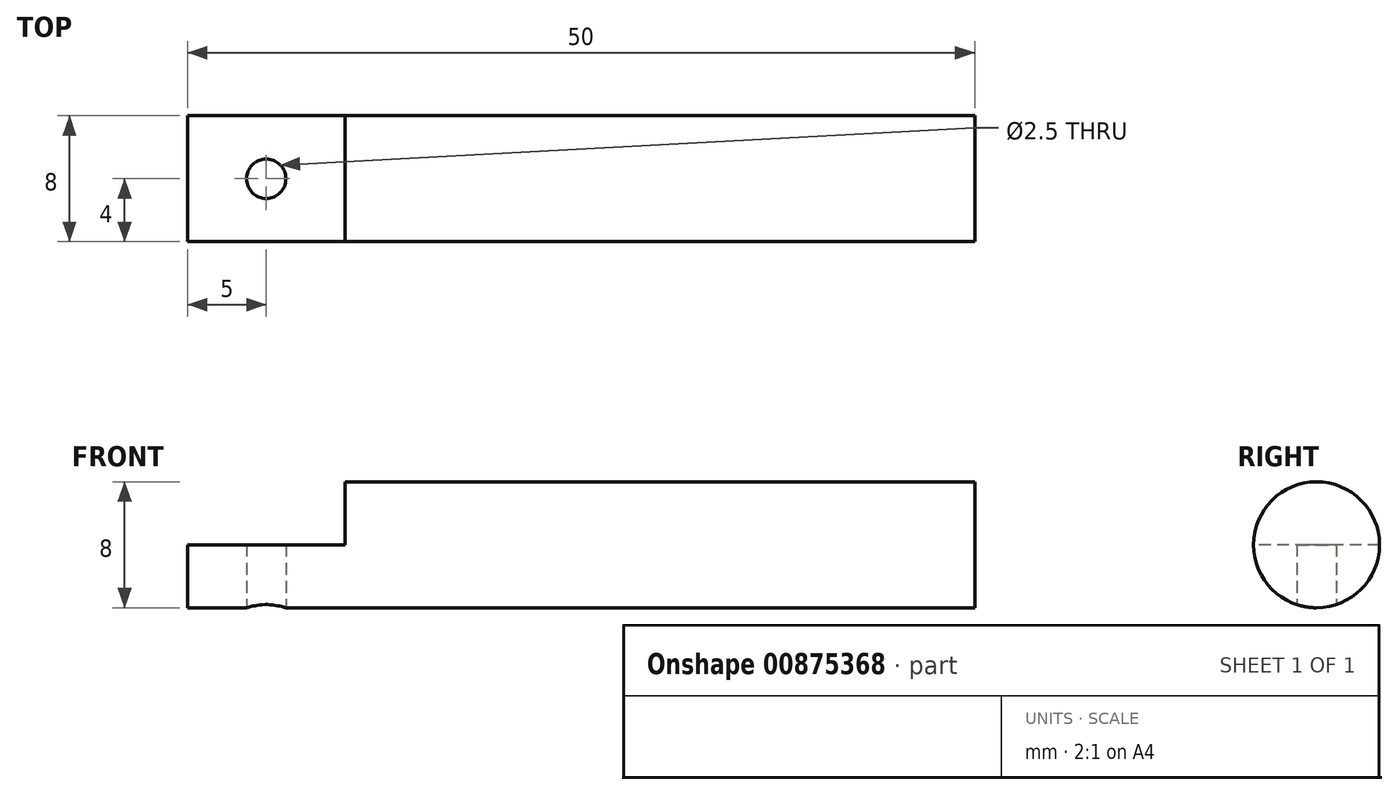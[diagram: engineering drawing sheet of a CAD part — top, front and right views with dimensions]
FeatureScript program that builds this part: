
annotation { "Feature Type Name" : "Feature", "Feature Type Description" : "" }
export const myFeature = defineFeature(function(context is Context, id is Id, definition is map)
    precondition{}
    {
        {
            var Q0;
            Q0=qCreatedBy(makeId("Right.planeOp"),FACE);
            var sketch = newSketch(context, id + "F0", { "sketchPlane" : qUnion([Q0])});
            skCircle(sketch, "E0", {"center": v(0, 0) * mm, "radius": 4 * mm});
            skSolve(sketch);
        }
        {
            var Q0;
            Q0=makeQuery(id+"F0.imprint","IMPRINT",FACE,{"disambiguationData":[TD([[makeQuery(id+"F0.imprint","IMPRINT",EDGE,{"derivedFrom":sQuery(id+"F0.wireOp",EDGE,"E0")}),1.0]])]});
            extrude(context, id + "F1", {"entities" : qUnion([Q0]), "depth" : 40 * mm, "offsetDistance" : 25 * mm});
        }
        {
            var Q0;
            Q0=makeQuery(id+"F1.opExtrude","CAP_FACE",FACE,{"disambiguationData":[OSD([sQuery(id+"F0.wireOp",EDGE,"E0")])],"isStart":true});
            var sketch = newSketch(context, id + "F2", { "sketchPlane" : qUnion([Q0])});
            skLineSegment(sketch, "E1", {"start": v(-4, 0) * mm, "end": v(4, 0) * mm});
            skPoint(sketch, "E2", {"position": v(0, -4) * mm});
            skArc(sketch, "E3", {"start": v(-4, 0) * mm, "mid": v(0, -4) * mm, "end": v(4, 0) * mm});
            skSolve(sketch);
        }
        {
            var Q0;
            Q0=makeQuery(id+"F2.imprint","IMPRINT",FACE,{"disambiguationData":[TD([[makeQuery(id+"F2.imprint","IMPRINT",EDGE,{"derivedFrom":sQuery(id+"F2.wireOp",EDGE,"E1")}),-1.0]])]});
            extrude(context, id + "F3", {"entities" : qUnion([Q0]), "operationType" : NewBodyOperationType.ADD, "depth" : 10 * mm, "offsetDistance" : 25 * mm});
        }
        {
            var Q0;
            Q0=makeQuery(id+"F3.opExtrude","SWEPT_FACE",FACE,{"disambiguationData":[OSD([sQuery(id+"F2.wireOp",EDGE,"E1")])]});
            var sketch = newSketch(context, id + "F4", { "sketchPlane" : qUnion([Q0])});
            skLineSegment(sketch, "E4", {"start": v(0, 4) * mm, "end": v(-10, -4) * mm, "construction": true});
            skLineSegment(sketch, "E5", {"start": v(-10, 4) * mm, "end": v(0, -4) * mm, "construction": true});
            skPoint(sketch, "E6", {"position": v(-5, 0) * mm});
            skSolve(sketch);
        }
        {
            var Q0;
            Q0=sQuery(id+"F4.wireOp",VERTEX,"E6");
            var Q1;
            Q1=makeQuery(id+"F1.opExtrude","SWEPT_BODY",BODY,{"disambiguationData":[OSD([sQuery(id+"F0.wireOp",EDGE,"E0")])]});
            hole(context, id + "F5", {"style" : HoleStyle.SIMPLE, "endStyle" : HoleEndStyle.THROUGH, "standardTappedOrClearance" : lookupTablePath({ "standard" : "ISO", "engagement" : "75%", "pitch" : "0.5 mm", "size" : "M3", "type" : "Tapped" }), "standardBlindInLast" : lookupTablePath({ "standard" : "ISO", "fit" : "Normal", "engagement" : "75%", "pitch" : "0.5 mm", "size" : "M3", "type" : "Clearance & tapped" }), "holeDiameter" : 2.5 * mm, "majorDiameter" : 3 * mm, "showTappedDepth" : true, "isTappedThrough" : true, "tappedDepth" : 12 * mm, "tapClearance" : 3, "locations" : qUnion([Q0]), "scope" : qUnion([Q1]), "startStyle" : HoleStartStyle.SKETCH});
        }
    });
